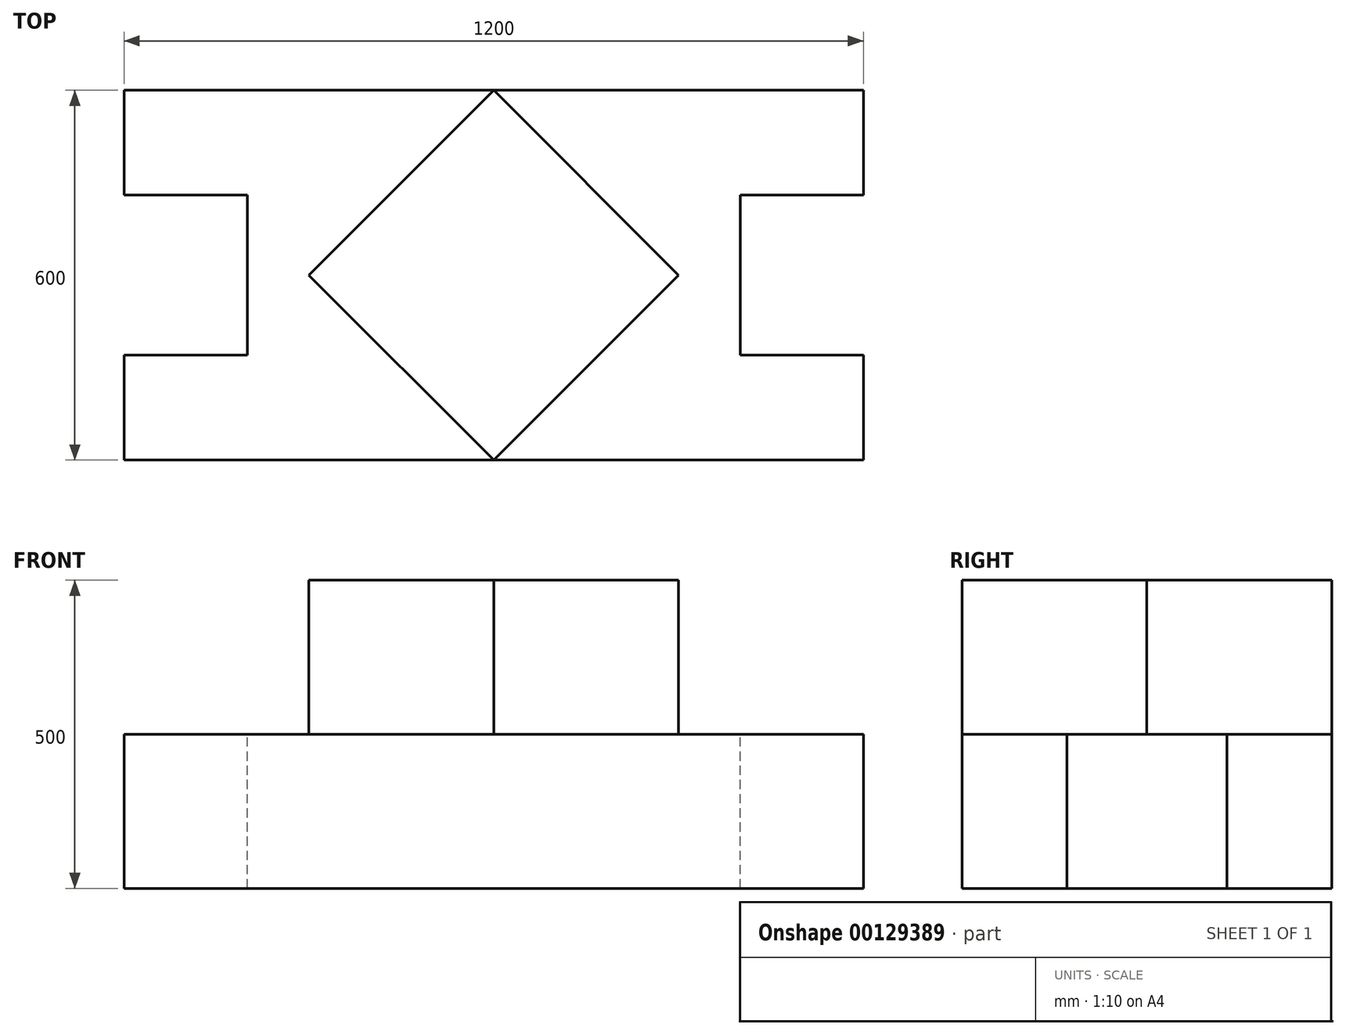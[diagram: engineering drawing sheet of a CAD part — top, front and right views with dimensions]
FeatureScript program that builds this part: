
annotation { "Feature Type Name" : "Feature", "Feature Type Description" : "" }
export const myFeature = defineFeature(function(context is Context, id is Id, definition is map)
    precondition{}
    {
        {
            var Q0;
            Q0=qCreatedBy(makeId("Top.planeOp"),FACE);
            var sketch = newSketch(context, id + "F0", { "sketchPlane" : qUnion([Q0])});
            skLineSegment(sketch, "E0.bottom", {"start": v(600, -300) * mm, "end": v(-600, -300) * mm});
            skLineSegment(sketch, "E0.top", {"start": v(600, 300) * mm, "end": v(-600, 300) * mm});
            skLineSegment(sketch, "E0.left", {"start": v(600, -300) * mm, "end": v(600, 300) * mm});
            skLineSegment(sketch, "E0.right", {"start": v(-600, -300) * mm, "end": v(-600, 300) * mm});
            skPoint(sketch, "E0.middle", {"position": v(0, 0) * mm});
            skSolve(sketch);
        }
        {
            var Q0;
            Q0 = qSketchRegion(id + "F0", true);
            extrude(context, id + "F1", {"entities" : qUnion([Q0]), "depth" : 250 * mm});
        }
        {
            var Q0;
            Q0=makeQuery(id+"F1.opExtrude","CAP_FACE",FACE,{"disambiguationData":[OSD([sQuery(id+"F0.wireOp",EDGE,"E0.bottom"),sQuery(id+"F0.wireOp",EDGE,"E0.top"),sQuery(id+"F0.wireOp",EDGE,"E0.left"),sQuery(id+"F0.wireOp",EDGE,"E0.right")])],"isStart":false});
            var sketch = newSketch(context, id + "F2", { "sketchPlane" : qUnion([Q0])});
            skLineSegment(sketch, "E1", {"start": v(0, 300) * mm, "end": v(-300, 0) * mm});
            skLineSegment(sketch, "E2", {"start": v(-300, 0) * mm, "end": v(0, -300) * mm});
            skLineSegment(sketch, "E3", {"start": v(0, -300) * mm, "end": v(300, 0) * mm});
            skLineSegment(sketch, "E4", {"start": v(300, 0) * mm, "end": v(0, 300) * mm});
            skSolve(sketch);
        }
        {
            var Q0;
            Q0 = qSketchRegion(id + "F2", true);
            extrude(context, id + "F3", {"entities" : qUnion([Q0]), "operationType" : NewBodyOperationType.ADD, "depth" : 250 * mm});
        }
        {
            var Q0;
            {var subQ0=sQuery(id+"F0.wireOp",EDGE,"E0.right");var subQ1=sQuery(id+"F0.wireOp",EDGE,"E0.top");var subQ2=sQuery(id+"F0.wireOp",EDGE,"E0.bottom");var subQ3=makeQuery(id+"F1.opExtrude","CAP_FACE",FACE,{"disambiguationData":[OSD([subQ2,subQ1,sQuery(id+"F0.wireOp",EDGE,"E0.left"),subQ0])],"isStart":false});Q0=makeQuery(id+"F3.boolean.opBoolean","SPLIT",FACE,{"disambiguationData":[TD([makeQuery(id+"F1.opExtrude","SWEPT_FACE",FACE,{"disambiguationData":[OSD([subQ0])]})])],"derivedFrom":subQ3});}
            var sketch = newSketch(context, id + "F4", { "sketchPlane" : qUnion([Q0])});
            skLineSegment(sketch, "E5.bottom", {"start": v(-400, -130) * mm, "end": v(-800, -130) * mm});
            skLineSegment(sketch, "E5.top", {"start": v(-400, 130) * mm, "end": v(-800, 130) * mm});
            skLineSegment(sketch, "E5.left", {"start": v(-400, -130) * mm, "end": v(-400, 130) * mm});
            skLineSegment(sketch, "E5.right", {"start": v(-800, -130) * mm, "end": v(-800, 130) * mm});
            skPoint(sketch, "E5.middle", {"position": v(-600, 0) * mm});
            skSolve(sketch);
        }
        {
            var Q0;
            Q0 = qSketchRegion(id + "F4", true);
            extrude(context, id + "F5", {"entities" : qUnion([Q0]), "operationType" : NewBodyOperationType.REMOVE, "endBound" : BoundingType.THROUGH_ALL, "oppositeDirection" : true, "depth" : 25 * mm});
        }
        {
            var Q0;
            {var subQ0=sQuery(id+"F0.wireOp",EDGE,"E0.left");var subQ1=sQuery(id+"F0.wireOp",EDGE,"E0.top");var subQ2=sQuery(id+"F0.wireOp",EDGE,"E0.bottom");var subQ3=makeQuery(id+"F1.opExtrude","CAP_FACE",FACE,{"disambiguationData":[OSD([subQ2,subQ1,subQ0,sQuery(id+"F0.wireOp",EDGE,"E0.right")])],"isStart":false});Q0=makeQuery(id+"F3.boolean.opBoolean","SPLIT",FACE,{"disambiguationData":[TD([makeQuery(id+"F1.opExtrude","SWEPT_FACE",FACE,{"disambiguationData":[OSD([subQ0])]})])],"derivedFrom":subQ3});}
            var sketch = newSketch(context, id + "F6", { "sketchPlane" : qUnion([Q0])});
            skLineSegment(sketch, "E6.bottom", {"start": v(800, -130) * mm, "end": v(400, -130) * mm});
            skLineSegment(sketch, "E6.top", {"start": v(800, 130) * mm, "end": v(400, 130) * mm});
            skLineSegment(sketch, "E6.left", {"start": v(800, -130) * mm, "end": v(800, 130) * mm});
            skLineSegment(sketch, "E6.right", {"start": v(400, -130) * mm, "end": v(400, 130) * mm});
            skPoint(sketch, "E6.middle", {"position": v(600, 0) * mm});
            skSolve(sketch);
        }
        {
            var Q0;
            Q0 = qSketchRegion(id + "F6", true);
            extrude(context, id + "F7", {"entities" : qUnion([Q0]), "operationType" : NewBodyOperationType.REMOVE, "endBound" : BoundingType.THROUGH_ALL, "oppositeDirection" : true, "depth" : 25 * mm});
        }
    });
